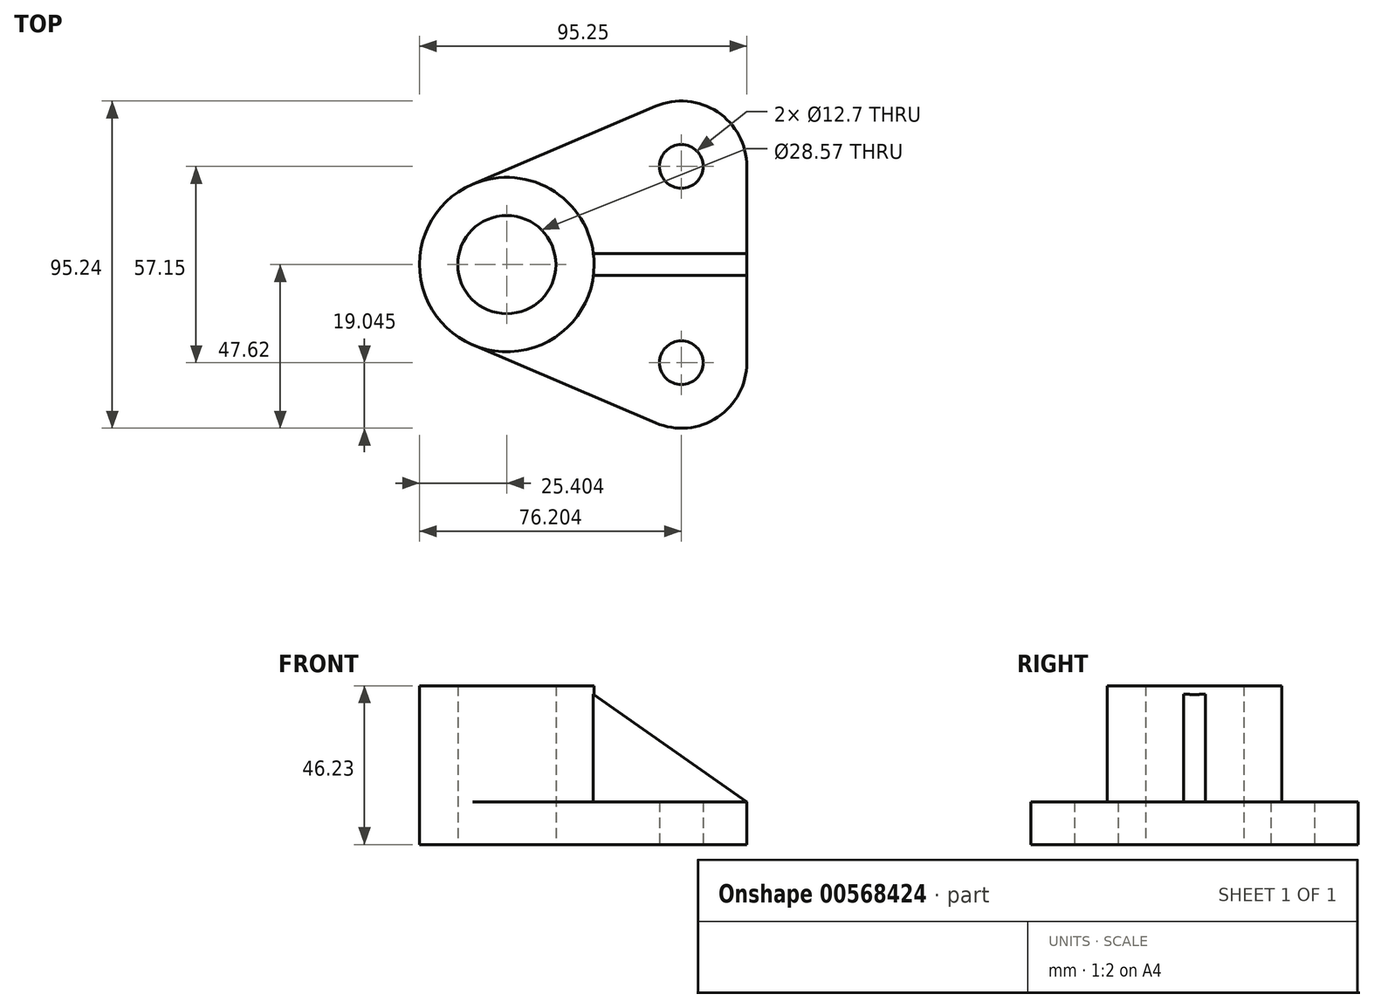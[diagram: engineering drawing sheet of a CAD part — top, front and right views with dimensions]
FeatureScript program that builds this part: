
annotation { "Feature Type Name" : "Feature", "Feature Type Description" : "" }
export const myFeature = defineFeature(function(context is Context, id is Id, definition is map)
    precondition{}
    {
        {
            var Q0;
            Q0=qCreatedBy(makeId("Top.planeOp"),FACE);
            var sketch = newSketch(context, id + "F0", { "sketchPlane" : qUnion([Q0])});
            skCircle(sketch, "E0", {"center": v(-40.57, 0) * mm, "radius": 14.29 * mm});
            skCircle(sketch, "E1", {"center": v(10.23, 28.57) * mm, "radius": 6.35 * mm});
            skCircle(sketch, "E2.MirrorC", {"center": v(10.23, -28.57) * mm, "radius": 6.35 * mm});
            skArc(sketch, "E3", {"start": v(29.28, 28.58) * mm, "mid": v(20.73, 44.47) * mm, "end": v(2.76, 46.1) * mm});
            skArc(sketch, "E4", {"start": v(2.76, -46.1) * mm, "mid": v(20.73, -44.47) * mm, "end": v(29.28, -28.58) * mm});
            skLineSegment(sketch, "E5", {"start": v(-50.53, 23.36) * mm, "end": v(2.76, 46.1) * mm});
            skLineSegment(sketch, "E6", {"start": v(29.28, 28.58) * mm, "end": v(29.28, 0) * mm});
            skLineSegment(sketch, "E7", {"start": v(29.28, 0) * mm, "end": v(29.28, -28.58) * mm});
            skLineSegment(sketch, "E8", {"start": v(2.76, -46.1) * mm, "end": v(-50.53, -23.36) * mm});
            skLineSegment(sketch, "E9.left", {"start": v(26.1, 3.17) * mm, "end": v(26.1, 0) * mm});
            skArc(sketch, "E10", {"start": v(-65.97, 0) * mm, "mid": v(-40.57, -25.4) * mm, "end": v(-15.17, 0) * mm});
            skArc(sketch, "E11", {"start": v(-15.17, 0) * mm, "mid": v(-40.57, 25.4) * mm, "end": v(-65.97, 0) * mm});
            skLineSegment(sketch, "E12", {"start": v(26.1, 0) * mm, "end": v(26.1, -3.18) * mm});
            skSolve(sketch);
        }
        {
            var Q0;
            Q0=makeQuery(id+"F0.imprint","IMPRINT",FACE,{"disambiguationData":[TD([[makeQuery(id+"F0.imprint","IMPRINT",EDGE,{"derivedFrom":sQuery(id+"F0.wireOp",EDGE,"E0")}),-1.0]])]});
            extrude(context, id + "F1", {"entities" : qUnion([Q0]), "depth" : 46.23 * mm, "offsetDistance" : 25.4 * mm});
        }
        {
            var Q0;
            Q0=makeQuery(id+"F0.imprint","IMPRINT",FACE,{"disambiguationData":[TD([[makeQuery(id+"F0.imprint","IMPRINT",EDGE,{"derivedFrom":sQuery(id+"F0.wireOp",EDGE,"E1")}),-1.0]])]});
            extrude(context, id + "F2", {"entities" : qUnion([Q0]), "operationType" : NewBodyOperationType.ADD, "depth" : 12.45 * mm, "offsetDistance" : 25.4 * mm});
        }
        {
            var Q0;
            Q0=qCreatedBy(makeId("Front.planeOp"),FACE);
            var sketch = newSketch(context, id + "F3", { "sketchPlane" : qUnion([Q0])});
            skLineSegment(sketch, "E13", {"start": v(-18.77, 46.23) * mm, "end": v(-18.77, 12.45) * mm});
            skLineSegment(sketch, "E14", {"start": v(-18.77, 12.45) * mm, "end": v(29.28, 12.45) * mm});
            skLineSegment(sketch, "E15", {"start": v(29.28, 12.45) * mm, "end": v(-18.77, 46.23) * mm});
            skSolve(sketch);
        }
        {
            var Q0;
            Q0=makeQuery(id+"F3.imprint","IMPRINT",FACE,{"disambiguationData":[TD([[makeQuery(id+"F3.imprint","IMPRINT",EDGE,{"derivedFrom":sQuery(id+"F3.wireOp",EDGE,"E13")}),1.0]])]});
            extrude(context, id + "F4", {"entities" : qUnion([Q0]), "operationType" : NewBodyOperationType.ADD, "endBound" : BoundingType.SYMMETRIC, "depth" : 6.35 * mm, "offsetDistance" : 25.4 * mm});
        }
    });
